# Revit family: Haworth_Epure_ErgonomicReturnDesk_EU_PRELIMINARY
name_source: partatom
category: Furniture
units: mm (PartAtom-declared; Revit-internal decimal feet)

## family parameters
Always vertical = Yes
Cut with Voids When Loaded = No
OmniClass Number = 23.40.70.14.64.11
OmniClass Title = Office Furniture
Room Calculation Point = No
Shared = No
Work Plane-Based = No

## types (4) — shared parameters
Actual Depth = 60 cm
Actual Height = 73 cm
Assembly Code = E2020200
Description = Haworth - Epure - Ergonomic Return Desk
Leg Height = 70 cm
Manufacturer = Haworth
Model = EUERXX06
Revision Number = 1
Size = Verify Final Dim.w/ Haworth
Trim Finish = Haworth _ Metal _ Structured White EC
URL = https://www.haworth.com
URL - Product = https://www.haworth.com
Warranty = http://www.haworth.com

## per-type parameters (varying)
| type | Actual Width | Rectangle Large | Rectangle Small | Rounded Large | Rounded Small |
| 80 x 60 - Rounded | 100 cm | No | No | No | Yes |
| 100 x 60 - Rounded | 100 cm | No | No | Yes | No |
| 100 x 60 - Rectangle | 100 cm | Yes | No | No | No |
| 80 x 60 - Rectangle | 80 cm | No | Yes | No | No |

## geometry (parser evidence)
native form markers: Blend x4, Sweep x10
no freeform markers — native parametric forms only
